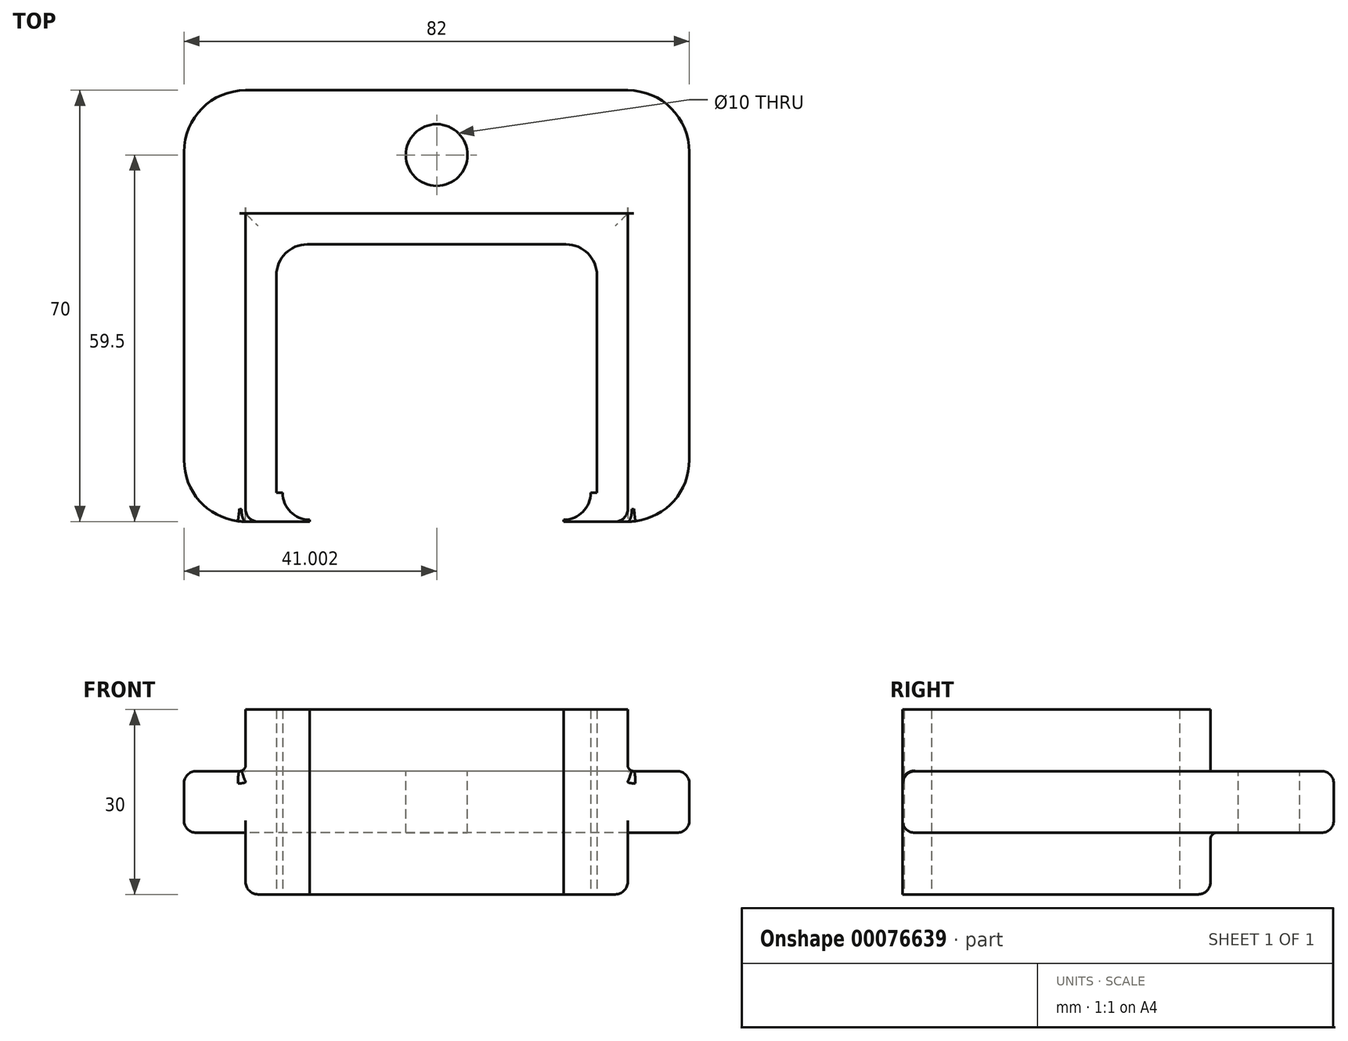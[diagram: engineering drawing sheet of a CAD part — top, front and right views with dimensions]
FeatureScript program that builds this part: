
annotation { "Feature Type Name" : "Feature", "Feature Type Description" : "" }
export const myFeature = defineFeature(function(context is Context, id is Id, definition is map)
    precondition{}
    {
        {
            var Q0;
            Q0=qCreatedBy(makeId("Top.planeOp"),FACE);
            var sketch = newSketch(context, id + "F0", { "sketchPlane" : qUnion([Q0])});
            skLineSegment(sketch, "E0", {"start": v(-10.72, 4.7) * mm, "end": v(-10.72, 45) * mm});
            skLineSegment(sketch, "E1", {"start": v(-10.72, 45) * mm, "end": v(41.28, 45) * mm});
            skLineSegment(sketch, "E2", {"start": v(41.28, 45) * mm, "end": v(41.28, 4.7) * mm});
            skLineSegment(sketch, "E3", {"start": v(41.28, 0) * mm, "end": v(46.28, 0) * mm});
            skLineSegment(sketch, "E4", {"start": v(46.28, 0) * mm, "end": v(46.28, 50) * mm});
            skLineSegment(sketch, "E5", {"start": v(46.28, 50) * mm, "end": v(-15.72, 50) * mm});
            skLineSegment(sketch, "E6", {"start": v(-15.72, 50) * mm, "end": v(-15.72, 0) * mm});
            skLineSegment(sketch, "E7", {"start": v(-15.72, 0) * mm, "end": v(-10.72, 0) * mm});
            skLineSegment(sketch, "E8", {"start": v(-10.72, 0) * mm, "end": v(-5.33, 0) * mm});
            skLineSegment(sketch, "E9", {"start": v(41.28, 0) * mm, "end": v(35.89, 0) * mm});
            skLineSegment(sketch, "E10", {"start": v(-5.33, 0) * mm, "end": v(-5.33, 0.3) * mm});
            skLineSegment(sketch, "E11", {"start": v(-9.72, 4.7) * mm, "end": v(-10.72, 4.7) * mm});
            skLineSegment(sketch, "E12", {"start": v(35.89, 0) * mm, "end": v(35.89, 0.3) * mm});
            skLineSegment(sketch, "E13", {"start": v(40.28, 4.7) * mm, "end": v(41.28, 4.7) * mm});
            skArc(sketch, "E14", {"start": v(-9.72, 4.7) * mm, "mid": v(-8.43, 1.59) * mm, "end": v(-5.33, 0.3) * mm});
            skArc(sketch, "E15", {"start": v(35.89, 0.3) * mm, "mid": v(39, 1.59) * mm, "end": v(40.28, 4.7) * mm});
            skSolve(sketch);
        }
        {
            var Q0;
            Q0=makeQuery(id+"F0.imprint","IMPRINT",FACE,{"disambiguationData":[TD([[makeQuery(id+"F0.imprint","IMPRINT",EDGE,{"derivedFrom":sQuery(id+"F0.wireOp",EDGE,"E0")}),1.0]])]});
            extrude(context, id + "F1", {"entities" : qUnion([Q0]), "depth" : 30 * mm});
        }
        {
            var Q0;
            Q0=makeQuery(id+"F1.opExtrude","SWEPT_FACE",FACE,{"disambiguationData":[OSD([sQuery(id+"F0.wireOp",EDGE,"E4")])]});
            var sketch = newSketch(context, id + "F2", { "sketchPlane" : qUnion([Q0])});
            skLineSegment(sketch, "E16", {"start": v(50, 10) * mm, "end": v(0, 10) * mm});
            skLineSegment(sketch, "E17", {"start": v(50, 20) * mm, "end": v(0, 20) * mm});
            skLineSegment(sketch, "E18", {"start": v(50, 10) * mm, "end": v(70, 10) * mm});
            skLineSegment(sketch, "E19", {"start": v(70, 10) * mm, "end": v(70, 20) * mm});
            skLineSegment(sketch, "E20", {"start": v(70, 20) * mm, "end": v(50, 20) * mm});
            skSolve(sketch);
        }
        {
            var Q0;
            {var subQ0=sQuery(id+"F2.wireOp",EDGE,"E16");Q0=makeQuery(id+"F2.imprint","IMPRINT",FACE,{"disambiguationData":[TD([[makeQuery(id+"F2.imprint","IMPRINT",EDGE,{"derivedFrom":subQ0}),-1.0]])]});}
            var Q1;
            {var subQ0=sQuery(id+"F2.wireOp",EDGE,"E18");Q1=makeQuery(id+"F2.imprint","IMPRINT",FACE,{"disambiguationData":[TD([[makeQuery(id+"F2.imprint","IMPRINT",EDGE,{"derivedFrom":subQ0}),1.0]])]});}
            extrude(context, id + "F3", {"entities" : qUnion([Q0, Q1]), "operationType" : NewBodyOperationType.ADD, "depth" : 10 * mm});
        }
        {
            var Q0;
            Q0=makeQuery(id+"F1.opExtrude","SWEPT_FACE",FACE,{"disambiguationData":[OSD([sQuery(id+"F0.wireOp",EDGE,"E6")])]});
            var sketch = newSketch(context, id + "F4", { "sketchPlane" : qUnion([Q0])});
            skLineSegment(sketch, "E21", {"start": v(0, 10) * mm, "end": v(-50, 10) * mm});
            skLineSegment(sketch, "E22", {"start": v(0, 20) * mm, "end": v(-50, 20) * mm});
            skLineSegment(sketch, "E23", {"start": v(-50, 10) * mm, "end": v(-70, 10) * mm});
            skLineSegment(sketch, "E24", {"start": v(-70, 10) * mm, "end": v(-70, 20) * mm});
            skLineSegment(sketch, "E25", {"start": v(-70, 20) * mm, "end": v(-50, 20) * mm});
            skSolve(sketch);
        }
        {
            var Q0;
            {var subQ0=sQuery(id+"F4.wireOp",EDGE,"E21");Q0=makeQuery(id+"F4.imprint","IMPRINT",FACE,{"disambiguationData":[TD([[makeQuery(id+"F4.imprint","IMPRINT",EDGE,{"derivedFrom":subQ0}),-1.0]])]});}
            var Q1;
            {var subQ0=sQuery(id+"F4.wireOp",EDGE,"E23");Q1=makeQuery(id+"F4.imprint","IMPRINT",FACE,{"disambiguationData":[TD([[makeQuery(id+"F4.imprint","IMPRINT",EDGE,{"derivedFrom":subQ0}),-1.0]])]});}
            extrude(context, id + "F5", {"entities" : qUnion([Q0, Q1]), "operationType" : NewBodyOperationType.ADD, "depth" : 10 * mm});
        }
        {
            var Q0;
            Q0=makeQuery(id+"F1.opExtrude","SWEPT_FACE",FACE,{"disambiguationData":[OSD([sQuery(id+"F0.wireOp",EDGE,"E5")])]});
            var sketch = newSketch(context, id + "F6", { "sketchPlane" : qUnion([Q0])});
            skLineSegment(sketch, "E26", {"start": v(-46.28, 20) * mm, "end": v(15.72, 20) * mm});
            skLineSegment(sketch, "E27", {"start": v(-46.28, 10) * mm, "end": v(15.72, 10) * mm});
            skSolve(sketch);
        }
        {
            var Q0;
            Q0=makeQuery(id+"F6.imprint","IMPRINT",FACE,{"disambiguationData":[TD([[makeQuery(id+"F6.imprint","IMPRINT",EDGE,{"derivedFrom":sQuery(id+"F6.wireOp",EDGE,"E26")}),-1.0]])]});
            extrude(context, id + "F7", {"entities" : qUnion([Q0]), "operationType" : NewBodyOperationType.ADD, "depth" : 20 * mm});
        }
        {
            var Q0;
            Q0=makeQuery(id+"F3.opExtrude","CAP_EDGE",EDGE,{"disambiguationData":[OSD([sQuery(id+"F0.wireOp",EDGE,"E3"),sQuery(id+"F0.wireOp",EDGE,"E4")])],"isStart":false});
            var Q1;
            Q1=makeQuery(id+"F5.opExtrude","CAP_EDGE",EDGE,{"disambiguationData":[OSD([sQuery(id+"F0.wireOp",EDGE,"E6"),sQuery(id+"F0.wireOp",EDGE,"E7")])],"isStart":false});
            var Q2;
            Q2=makeQuery(id+"F3.opExtrude","CAP_EDGE",EDGE,{"disambiguationData":[OSD([sQuery(id+"F2.wireOp",EDGE,"E19")])],"isStart":false});
            var Q3;
            Q3=makeQuery(id+"F5.opExtrude","CAP_EDGE",EDGE,{"disambiguationData":[OSD([sQuery(id+"F4.wireOp",EDGE,"E24")])],"isStart":false});
            fillet(context, id + "F8", {"entities" : qUnion([Q0, Q1, Q2, Q3]), "radius" : 10 * mm, "tangentPropagation" : true, "allowEdgeOverflow" : false});
        }
        {
            var Q0;
            {var subQ0=sQuery(id+"F2.wireOp",EDGE,"E20");var subQ1=sQuery(id+"F2.wireOp",EDGE,"E17");var subQ3=sQuery(id+"F0.wireOp",EDGE,"E3");Q0=makeQuery(id+"F3.boolean.opBoolean","SPLIT",EDGE,{"disambiguationData":[TD([makeQuery(id+"F1.opExtrude","SWEPT_FACE",FACE,{"disambiguationData":[OSD([subQ3,sQuery(id+"F0.wireOp",EDGE,"E9")])]})])],"derivedFrom":makeQuery(id+"F3.opExtrude","CAP_EDGE",EDGE,{"disambiguationData":[OSD([subQ1,subQ0])],"isStart":true})});}
            var Q1;
            Q1=makeQuery(id+"F7.opExtrude","CAP_EDGE",EDGE,{"disambiguationData":[OSD([sQuery(id+"F6.wireOp",EDGE,"E26")])],"isStart":true});
            var Q2;
            {var subQ0=sQuery(id+"F4.wireOp",EDGE,"E25");var subQ1=sQuery(id+"F4.wireOp",EDGE,"E22");var subQ2=sQuery(id+"F0.wireOp",EDGE,"E7");Q2=makeQuery(id+"F5.boolean.opBoolean","SPLIT",EDGE,{"disambiguationData":[TD([makeQuery(id+"F1.opExtrude","SWEPT_FACE",FACE,{"disambiguationData":[OSD([subQ2,sQuery(id+"F0.wireOp",EDGE,"E8")])]})])],"derivedFrom":makeQuery(id+"F5.opExtrude","CAP_EDGE",EDGE,{"disambiguationData":[OSD([subQ1,subQ0])],"isStart":true})});}
            var Q3;
            {var subQ0=sQuery(id+"F4.wireOp",EDGE,"E23");var subQ1=sQuery(id+"F4.wireOp",EDGE,"E21");var subQ2=sQuery(id+"F0.wireOp",EDGE,"E7");Q3=makeQuery(id+"F5.boolean.opBoolean","SPLIT",EDGE,{"disambiguationData":[TD([makeQuery(id+"F1.opExtrude","SWEPT_FACE",FACE,{"disambiguationData":[OSD([subQ2,sQuery(id+"F0.wireOp",EDGE,"E8")])]})])],"derivedFrom":makeQuery(id+"F5.opExtrude","CAP_EDGE",EDGE,{"disambiguationData":[OSD([subQ1,subQ0])],"isStart":true})});}
            var Q4;
            Q4=makeQuery(id+"F7.opExtrude","CAP_EDGE",EDGE,{"disambiguationData":[OSD([sQuery(id+"F6.wireOp",EDGE,"E27")])],"isStart":true});
            var Q5;
            {var subQ0=sQuery(id+"F2.wireOp",EDGE,"E18");var subQ1=sQuery(id+"F2.wireOp",EDGE,"E16");var subQ3=sQuery(id+"F0.wireOp",EDGE,"E3");Q5=makeQuery(id+"F3.boolean.opBoolean","SPLIT",EDGE,{"disambiguationData":[TD([makeQuery(id+"F1.opExtrude","SWEPT_FACE",FACE,{"disambiguationData":[OSD([subQ3,sQuery(id+"F0.wireOp",EDGE,"E9")])]})])],"derivedFrom":makeQuery(id+"F3.opExtrude","CAP_EDGE",EDGE,{"disambiguationData":[OSD([subQ1,subQ0])],"isStart":true})});}
            fillet(context, id + "F9", {"entities" : qUnion([Q0, Q1, Q2, Q3, Q4, Q5]), "radius" : 1 * mm, "tangentPropagation" : true, "allowEdgeOverflow" : false});
        }
        {
            var Q0;
            Q0=makeQuery(id+"F1.opExtrude","CAP_EDGE",EDGE,{"disambiguationData":[OSD([sQuery(id+"F0.wireOp",EDGE,"E6")])],"isStart":true});
            var Q1;
            Q1=makeQuery(id+"F1.opExtrude","CAP_EDGE",EDGE,{"disambiguationData":[OSD([sQuery(id+"F0.wireOp",EDGE,"E5")])],"isStart":true});
            var Q2;
            Q2=makeQuery(id+"F1.opExtrude","CAP_EDGE",EDGE,{"disambiguationData":[OSD([sQuery(id+"F0.wireOp",EDGE,"E4")])],"isStart":true});
            var Q3;
            Q3=makeQuery(id+"F8.opFillet","BLEND_EDGE",EDGE,{"blendedFrom":[makeQuery(id+"F3.opExtrude","CAP_EDGE",EDGE,{"disambiguationData":[OSD([sQuery(id+"F0.wireOp",EDGE,"E3"),sQuery(id+"F0.wireOp",EDGE,"E4")])],"isStart":false}),makeQuery(id+"F7.boolean.opBoolean","MERGE",FACE,{"derivedFrom":[makeQuery(id+"F3.opExtrude","SWEPT_FACE",FACE,{"disambiguationData":[OSD([sQuery(id+"F2.wireOp",EDGE,"E16"),sQuery(id+"F2.wireOp",EDGE,"E18")])]}),makeQuery(id+"F5.opExtrude","SWEPT_FACE",FACE,{"disambiguationData":[OSD([sQuery(id+"F4.wireOp",EDGE,"E21"),sQuery(id+"F4.wireOp",EDGE,"E23")])]}),makeQuery(id+"F7.opExtrude","SWEPT_FACE",FACE,{"disambiguationData":[OSD([sQuery(id+"F6.wireOp",EDGE,"E27")])]})]})],"blendedInto":[makeQuery(id+"F7.boolean.opBoolean","MERGE",FACE,{"derivedFrom":[makeQuery(id+"F3.opExtrude","SWEPT_FACE",FACE,{"disambiguationData":[OSD([sQuery(id+"F2.wireOp",EDGE,"E16"),sQuery(id+"F2.wireOp",EDGE,"E18")])]}),makeQuery(id+"F5.opExtrude","SWEPT_FACE",FACE,{"disambiguationData":[OSD([sQuery(id+"F4.wireOp",EDGE,"E21"),sQuery(id+"F4.wireOp",EDGE,"E23")])]}),makeQuery(id+"F7.opExtrude","SWEPT_FACE",FACE,{"disambiguationData":[OSD([sQuery(id+"F6.wireOp",EDGE,"E27")])]})]})]});
            var Q4;
            Q4=makeQuery(id+"F7.boolean.opBoolean","MERGE",EDGE,{"derivedFrom":[makeQuery(id+"F3.opExtrude","SWEPT_EDGE",EDGE,{"disambiguationData":[OSD([sQuery(id+"F2.wireOp",EDGE,"E19"),sQuery(id+"F2.wireOp",EDGE,"E20")])]}),makeQuery(id+"F5.opExtrude","SWEPT_EDGE",EDGE,{"disambiguationData":[OSD([sQuery(id+"F4.wireOp",EDGE,"E24"),sQuery(id+"F4.wireOp",EDGE,"E25")])]}),makeQuery(id+"F7.opExtrude","CAP_EDGE",EDGE,{"disambiguationData":[OSD([sQuery(id+"F6.wireOp",EDGE,"E26")])],"isStart":false})]});
            fillet(context, id + "F10", {"entities" : qUnion([Q0, Q1, Q2, Q3, Q4]), "radius" : 2 * mm, "tangentPropagation" : true, "allowEdgeOverflow" : false});
        }
        {
            var Q0;
            Q0=makeQuery(id+"F7.boolean.opBoolean","MERGE",FACE,{"derivedFrom":[makeQuery(id+"F3.opExtrude","SWEPT_FACE",FACE,{"disambiguationData":[OSD([sQuery(id+"F2.wireOp",EDGE,"E17"),sQuery(id+"F2.wireOp",EDGE,"E20")])]}),makeQuery(id+"F5.opExtrude","SWEPT_FACE",FACE,{"disambiguationData":[OSD([sQuery(id+"F4.wireOp",EDGE,"E22"),sQuery(id+"F4.wireOp",EDGE,"E25")])]}),makeQuery(id+"F7.opExtrude","SWEPT_FACE",FACE,{"disambiguationData":[OSD([sQuery(id+"F6.wireOp",EDGE,"E26")])]})]});
            var sketch = newSketch(context, id + "F11", { "sketchPlane" : qUnion([Q0])});
            skPoint(sketch, "E28", {"position": v(15.28, 59.5) * mm});
            skSolve(sketch);
        }
        {
            var Q0;
            Q0=sQuery(id+"F11.wireOp",VERTEX,"E28");
            var Q1;
            Q1=makeQuery(id+"F1.opExtrude","SWEPT_BODY",BODY,{"disambiguationData":[OSD([sQuery(id+"F0.wireOp",EDGE,"E0"),sQuery(id+"F0.wireOp",EDGE,"E1"),sQuery(id+"F0.wireOp",EDGE,"E2"),sQuery(id+"F0.wireOp",EDGE,"E3"),sQuery(id+"F0.wireOp",EDGE,"E4"),sQuery(id+"F0.wireOp",EDGE,"E5"),sQuery(id+"F0.wireOp",EDGE,"E6"),sQuery(id+"F0.wireOp",EDGE,"E7"),sQuery(id+"F0.wireOp",EDGE,"E8"),sQuery(id+"F0.wireOp",EDGE,"qnYStmg7-cNfN-4NJj-bSRZ-ppeeHPcSavuo"),sQuery(id+"F0.wireOp",EDGE,"E9"),sQuery(id+"F0.wireOp",EDGE,"mvlLx6JA-hAmw-UMoD-nlto-pv3sMWuoO2Pm")])]});
            hole(context, id + "F12", {"style" : HoleStyle.SIMPLE, "endStyle" : HoleEndStyle.THROUGH, "holeDiameter" : 10 * mm, "locations" : qUnion([Q0]), "scope" : qUnion([Q1]), "isTappedThrough" : true});
        }
        {
            var Q0;
            Q0=makeQuery(id+"F1.opExtrude","SWEPT_EDGE",EDGE,{"disambiguationData":[OSD([sQuery(id+"F0.wireOp",EDGE,"E0"),sQuery(id+"F0.wireOp",EDGE,"E1")])]});
            var Q1;
            Q1=makeQuery(id+"F1.opExtrude","SWEPT_EDGE",EDGE,{"disambiguationData":[OSD([sQuery(id+"F0.wireOp",EDGE,"E1"),sQuery(id+"F0.wireOp",EDGE,"E2")])]});
            fillet(context, id + "F13", {"entities" : qUnion([Q0, Q1]), "radius" : 5 * mm, "tangentPropagation" : true, "allowEdgeOverflow" : false});
        }
    });
